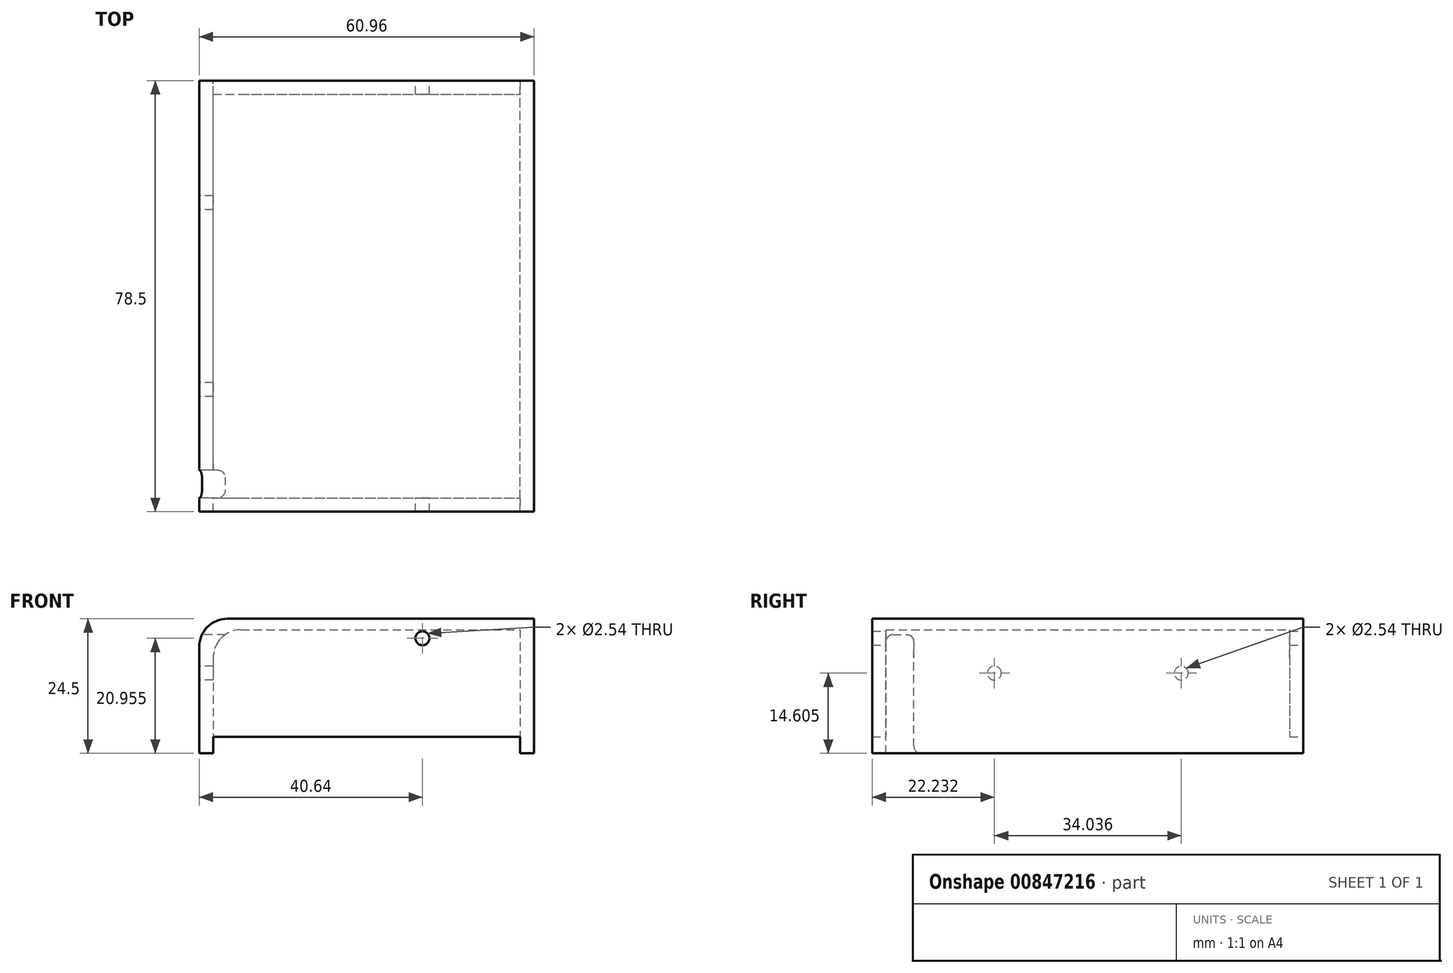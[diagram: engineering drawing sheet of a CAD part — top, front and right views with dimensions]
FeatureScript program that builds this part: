
annotation { "Feature Type Name" : "Feature", "Feature Type Description" : "" }
export const myFeature = defineFeature(function(context is Context, id is Id, definition is map)
    precondition{}
    {
        {
            var Q0;
            Q0=qCreatedBy(makeId("Top.planeOp"),FACE);
            var sketch = newSketch(context, id + "F0", { "sketchPlane" : qUnion([Q0])});
            skLineSegment(sketch, "E0.bottom", {"start": v(0, 0) * mm, "end": v(55.88, 0) * mm});
            skLineSegment(sketch, "E0.top", {"start": v(0, 73.5) * mm, "end": v(55.88, 73.5) * mm});
            skLineSegment(sketch, "E0.left", {"start": v(0, 0) * mm, "end": v(0, 73.5) * mm});
            skLineSegment(sketch, "E0.right", {"start": v(55.88, 0) * mm, "end": v(55.88, 73.5) * mm});
            skSolve(sketch);
        }
        {
            var Q0;
            Q0=qCreatedBy(makeId("Top.planeOp"),FACE);
            var sketch = newSketch(context, id + "F1", { "sketchPlane" : qUnion([Q0])});
            skLineSegment(sketch, "E1.bottom", {"start": v(-2.54, 76) * mm, "end": v(58.42, 76) * mm});
            skLineSegment(sketch, "E1.top", {"start": v(-2.54, -2.5) * mm, "end": v(58.42, -2.5) * mm});
            skLineSegment(sketch, "E1.left", {"start": v(-2.54, 76) * mm, "end": v(-2.54, -2.5) * mm});
            skLineSegment(sketch, "E1.right", {"start": v(58.42, 76) * mm, "end": v(58.42, -2.5) * mm});
            skSolve(sketch);
        }
        {
            var Q0;
            Q0=qSketchRegion(id+"F1",true);
            extrude(context, id + "F2", {"entities" : qUnion([Q0]), "depth" : 21.5 * mm, "offsetDistance" : 25 * mm});
        }
        {
            var Q0;
            Q0=qSketchRegion(id+"F0",true);
            extrude(context, id + "F3", {"entities" : qUnion([Q0]), "operationType" : NewBodyOperationType.REMOVE, "depth" : 19.5 * mm, "offsetDistance" : 25 * mm});
        }
        {
            var Q0;
            Q0=makeQuery(id+"F2.opExtrude","SWEPT_FACE",FACE,{"disambiguationData":[OSD([sQuery(id+"F1.wireOp",EDGE,"E1.right")])]});
            var sketch = newSketch(context, id + "F4", { "sketchPlane" : qUnion([Q0])});
            skLineSegment(sketch, "E2.bottom", {"start": v(-2.5, 0) * mm, "end": v(76, 0) * mm});
            skLineSegment(sketch, "E2.top", {"start": v(-2.5, -3) * mm, "end": v(76, -3) * mm});
            skLineSegment(sketch, "E2.left", {"start": v(-2.5, 0) * mm, "end": v(-2.5, -3) * mm});
            skLineSegment(sketch, "E2.right", {"start": v(76, 0) * mm, "end": v(76, -3) * mm});
            skSolve(sketch);
        }
        {
            var Q0;
            Q0=makeQuery(id+"F4.imprint","IMPRINT",FACE,{"disambiguationData":[TD([[makeQuery(id+"F4.imprint","IMPRINT",EDGE,{"derivedFrom":sQuery(id+"F4.wireOp",EDGE,"E2.bottom")}),1.0]])]});
            var Q1;
            Q1=makeQuery(id+"F3.boolean.opBoolean","COPY",FACE,{"derivedFrom":makeQuery(id+"F3.opExtrude","SWEPT_FACE",FACE,{"disambiguationData":[OSD([sQuery(id+"F0.wireOp",EDGE,"E0.right")])]})});
            extrude(context, id + "F5", {"entities" : qUnion([Q0]), "operationType" : NewBodyOperationType.ADD, "endBound" : BoundingType.UP_TO_SURFACE, "oppositeDirection" : true, "depth" : 25 * mm, "endBoundEntityFace" : qUnion([Q1]), "offsetDistance" : 25 * mm});
        }
        {
            var Q0;
            Q0=makeQuery(id+"F2.opExtrude","SWEPT_FACE",FACE,{"disambiguationData":[OSD([sQuery(id+"F1.wireOp",EDGE,"E1.left")])]});
            var sketch = newSketch(context, id + "F6", { "sketchPlane" : qUnion([Q0])});
            skLineSegment(sketch, "E3.bottom", {"start": v(-76, 0) * mm, "end": v(2.5, 0) * mm});
            skLineSegment(sketch, "E3.top", {"start": v(-76, -3) * mm, "end": v(2.5, -3) * mm});
            skLineSegment(sketch, "E3.left", {"start": v(-76, 0) * mm, "end": v(-76, -3) * mm});
            skLineSegment(sketch, "E3.right", {"start": v(2.5, 0) * mm, "end": v(2.5, -3) * mm});
            skSolve(sketch);
        }
        {
            var Q0;
            Q0=qSketchRegion(id+"F6",true);
            var Q1;
            Q1=makeQuery(id+"F3.boolean.opBoolean","COPY",FACE,{"derivedFrom":makeQuery(id+"F3.opExtrude","SWEPT_FACE",FACE,{"disambiguationData":[OSD([sQuery(id+"F0.wireOp",EDGE,"E0.left")])]})});
            var Q2;
            Q2=makeQuery(id+"F2.opExtrude","SWEPT_BODY",BODY,{"disambiguationData":[OSD([sQuery(id+"F1.wireOp",EDGE,"E1.bottom"),sQuery(id+"F1.wireOp",EDGE,"E1.top"),sQuery(id+"F1.wireOp",EDGE,"E1.left"),sQuery(id+"F1.wireOp",EDGE,"E1.right")])]});
            extrude(context, id + "F7", {"entities" : qUnion([Q0]), "operationType" : NewBodyOperationType.ADD, "endBound" : BoundingType.UP_TO_SURFACE, "oppositeDirection" : true, "depth" : 25 * mm, "endBoundEntityFace" : qUnion([Q1]), "endBoundEntityBody" : qUnion([Q2]), "offsetDistance" : 25 * mm});
        }
        {
            var Q0;
            Q0=makeQuery(id+"F7.boolean.opBoolean","MERGE",FACE,{"derivedFrom":[makeQuery(id+"F5.boolean.opBoolean","MERGE",FACE,{"derivedFrom":[makeQuery(id+"F2.opExtrude","SWEPT_FACE",FACE,{"disambiguationData":[OSD([sQuery(id+"F1.wireOp",EDGE,"E1.top")])]}),makeQuery(id+"F5.opExtrude","SWEPT_FACE",FACE,{"disambiguationData":[OSD([sQuery(id+"F4.wireOp",EDGE,"E2.left")])]})]}),makeQuery(id+"F7.opExtrude","SWEPT_FACE",FACE,{"disambiguationData":[OSD([sQuery(id+"F6.wireOp",EDGE,"E3.right")])]})]});
            var sketch = newSketch(context, id + "F8", { "sketchPlane" : qUnion([Q0])});
            skLineSegment(sketch, "E4.bottom", {"start": v(5.06, 12.2) * mm, "end": v(49.15, 12.2) * mm});
            skLineSegment(sketch, "E4.top", {"start": v(5.06, 4.75) * mm, "end": v(49.15, 4.75) * mm});
            skLineSegment(sketch, "E4.left", {"start": v(5.06, 12.2) * mm, "end": v(5.06, 4.75) * mm});
            skLineSegment(sketch, "E4.right", {"start": v(49.15, 12.2) * mm, "end": v(49.15, 4.75) * mm});
            skSolve(sketch);
        }
        {
            var Q0;
            Q0=qSketchRegion(id+"F8",true);
            var Q1;
            Q1=makeQuery(id+"F3.boolean.opBoolean","COPY",FACE,{"derivedFrom":makeQuery(id+"F3.opExtrude","SWEPT_FACE",FACE,{"disambiguationData":[OSD([sQuery(id+"F0.wireOp",EDGE,"E0.bottom")])]})});
            extrude(context, id + "F9", {"entities" : qUnion([Q0]), "operationType" : NewBodyOperationType.ADD, "endBound" : BoundingType.UP_TO_SURFACE, "oppositeDirection" : true, "depth" : 25 * mm, "endBoundEntityFace" : qUnion([Q1]), "offsetDistance" : 25 * mm});
        }
        {
            var Q0;
            Q0=makeQuery(id+"F7.boolean.opBoolean","MERGE",FACE,{"derivedFrom":[makeQuery(id+"F2.opExtrude","SWEPT_FACE",FACE,{"disambiguationData":[OSD([sQuery(id+"F1.wireOp",EDGE,"E1.left")])]}),makeQuery(id+"F7.opExtrude","CAP_FACE",FACE,{"disambiguationData":[OSD([sQuery(id+"F6.wireOp",EDGE,"E3.bottom"),sQuery(id+"F6.wireOp",EDGE,"E3.top"),sQuery(id+"F6.wireOp",EDGE,"E3.left"),sQuery(id+"F6.wireOp",EDGE,"E3.right")])],"isStart":true})]});
            var sketch = newSketch(context, id + "F10", { "sketchPlane" : qUnion([Q0])});
            skLineSegment(sketch, "E5.bottom", {"start": v(-5.08, -3) * mm, "end": v(0, -3) * mm});
            skLineSegment(sketch, "E5.top", {"start": v(-5.08, 18.59) * mm, "end": v(0, 18.59) * mm});
            skLineSegment(sketch, "E5.left", {"start": v(-5.08, -3) * mm, "end": v(-5.08, 18.59) * mm});
            skLineSegment(sketch, "E5.right", {"start": v(0, -3) * mm, "end": v(0, 18.59) * mm});
            skSolve(sketch);
        }
        {
            var Q0;
            Q0=qSketchRegion(id+"F10",true);
            extrude(context, id + "F11", {"entities" : qUnion([Q0]), "operationType" : NewBodyOperationType.REMOVE, "oppositeDirection" : true, "depth" : 25.4 * mm, "offsetDistance" : 25.4 * mm});
        }
        {
            var Q0;
            Q0=makeQuery(id+"F11.boolean.opBoolean","COPY",EDGE,{"derivedFrom":makeQuery(id+"F11.opExtrude","SWEPT_EDGE",EDGE,{"disambiguationData":[OSD([sQuery(id+"F6.wireOp",EDGE,"E3.top"),sQuery(id+"F10.wireOp",EDGE,"E5.bottom"),sQuery(id+"F10.wireOp",EDGE,"E5.right")])]})});
            var Q1;
            Q1=makeQuery(id+"F11.boolean.opBoolean","COPY",EDGE,{"derivedFrom":makeQuery(id+"F11.opExtrude","SWEPT_EDGE",EDGE,{"disambiguationData":[OSD([sQuery(id+"F6.wireOp",EDGE,"E3.top"),sQuery(id+"F10.wireOp",EDGE,"E5.bottom"),sQuery(id+"F10.wireOp",EDGE,"E5.left")])]})});
            fillet(context, id + "F12", {"entities" : qUnion([Q0, Q1]), "radius" : 1.27 * mm, "tangentPropagation" : true, "allowEdgeOverflow" : false});
        }
        {
            var Q0;
            Q0=makeQuery(id+"F7.boolean.opBoolean","MERGE",FACE,{"derivedFrom":[makeQuery(id+"F5.boolean.opBoolean","MERGE",FACE,{"derivedFrom":[makeQuery(id+"F2.opExtrude","SWEPT_FACE",FACE,{"disambiguationData":[OSD([sQuery(id+"F1.wireOp",EDGE,"E1.bottom")])]}),makeQuery(id+"F5.opExtrude","SWEPT_FACE",FACE,{"disambiguationData":[OSD([sQuery(id+"F4.wireOp",EDGE,"E2.right")])]})]}),makeQuery(id+"F7.opExtrude","SWEPT_FACE",FACE,{"disambiguationData":[OSD([sQuery(id+"F6.wireOp",EDGE,"E3.left")])]})]});
            var sketch = newSketch(context, id + "F13", { "sketchPlane" : qUnion([Q0])});
            skCircle(sketch, "E6", {"center": v(-38.1, 17.96) * mm, "radius": 1.27 * mm});
            skSolve(sketch);
        }
        {
            var Q0;
            Q0=qSketchRegion(id+"F13",true);
            extrude(context, id + "F14", {"entities" : qUnion([Q0]), "operationType" : NewBodyOperationType.REMOVE, "oppositeDirection" : true, "depth" : 101.6 * mm, "offsetDistance" : 25.4 * mm});
        }
        {
            var Q0;
            Q0=makeQuery(id+"F7.boolean.opBoolean","MERGE",FACE,{"derivedFrom":[makeQuery(id+"F2.opExtrude","SWEPT_FACE",FACE,{"disambiguationData":[OSD([sQuery(id+"F1.wireOp",EDGE,"E1.left")])]}),makeQuery(id+"F7.opExtrude","CAP_FACE",FACE,{"disambiguationData":[OSD([sQuery(id+"F6.wireOp",EDGE,"E3.bottom"),sQuery(id+"F6.wireOp",EDGE,"E3.top"),sQuery(id+"F6.wireOp",EDGE,"E3.left"),sQuery(id+"F6.wireOp",EDGE,"E3.right")])],"isStart":true})]});
            var sketch = newSketch(context, id + "F15", { "sketchPlane" : qUnion([Q0])});
            skCircle(sketch, "E7", {"center": v(-53.77, 11.6) * mm, "radius": 1.27 * mm});
            skLineSegment(sketch, "E8", {"start": v(-36.75, 21.5) * mm, "end": v(-36.75, -3) * mm, "construction": true});
            skCircle(sketch, "E9.MirrorC", {"center": v(-19.73, 11.6) * mm, "radius": 1.27 * mm});
            skSolve(sketch);
        }
        {
            var Q0;
            Q0=qSketchRegion(id+"F15",true);
            extrude(context, id + "F16", {"entities" : qUnion([Q0]), "operationType" : NewBodyOperationType.REMOVE, "oppositeDirection" : true, "depth" : 25.4 * mm, "offsetDistance" : 25.4 * mm});
        }
        {
            var Q0;
            Q0=makeQuery(id+"F11.boolean.opBoolean","COPY",EDGE,{"derivedFrom":makeQuery(id+"F11.opExtrude","SWEPT_EDGE",EDGE,{"disambiguationData":[OSD([sQuery(id+"F10.wireOp",EDGE,"E5.top"),sQuery(id+"F10.wireOp",EDGE,"E5.right")])]})});
            var Q1;
            Q1=makeQuery(id+"F11.boolean.opBoolean","COPY",EDGE,{"derivedFrom":makeQuery(id+"F11.opExtrude","SWEPT_EDGE",EDGE,{"disambiguationData":[OSD([sQuery(id+"F10.wireOp",EDGE,"E5.top"),sQuery(id+"F10.wireOp",EDGE,"E5.left")])]})});
            fillet(context, id + "F17", {"entities" : qUnion([Q0, Q1]), "radius" : 1.27 * mm, "tangentPropagation" : true, "allowEdgeOverflow" : false});
        }
        {
            var Q0;
            Q0=makeQuery(id+"F3.boolean.opBoolean","COPY",EDGE,{"derivedFrom":makeQuery(id+"F3.opExtrude","CAP_EDGE",EDGE,{"disambiguationData":[OSD([sQuery(id+"F0.wireOp",EDGE,"E0.left")])],"isStart":false})});
            var Q1;
            Q1=makeQuery(id+"F2.opExtrude","CAP_EDGE",EDGE,{"disambiguationData":[OSD([sQuery(id+"F1.wireOp",EDGE,"E1.left")])],"isStart":false});
            fillet(context, id + "F18", {"entities" : qUnion([Q0, Q1]), "radius" : 5.08 * mm, "tangentPropagation" : true, "allowEdgeOverflow" : false});
        }
    });
